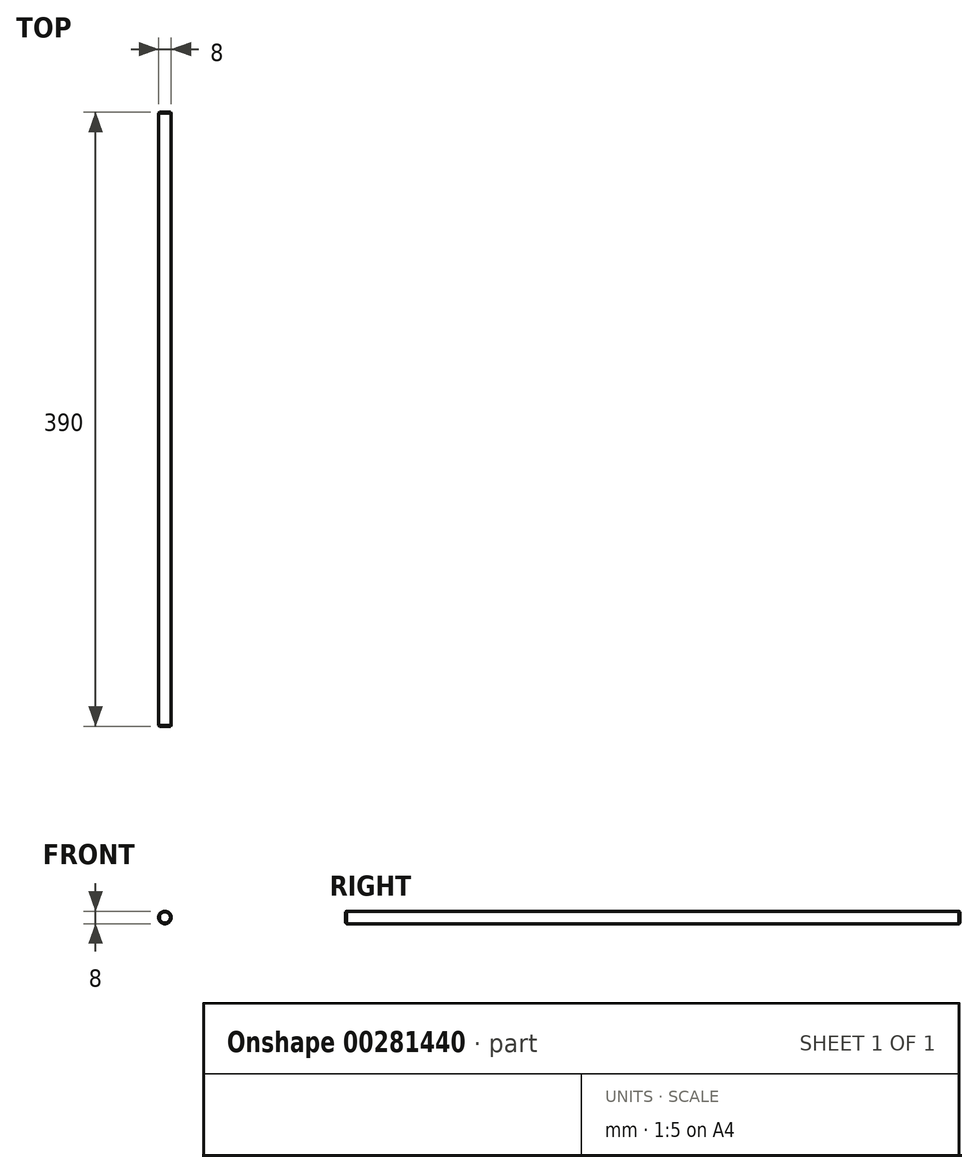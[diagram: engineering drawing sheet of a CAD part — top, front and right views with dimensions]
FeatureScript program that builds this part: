
annotation { "Feature Type Name" : "Feature", "Feature Type Description" : "" }
export const myFeature = defineFeature(function(context is Context, id is Id, definition is map)
    precondition{}
    {
        {
            var Q0;
            Q0=qCreatedBy(makeId("Front.planeOp"),FACE);
            var sketch = newSketch(context, id + "F0", { "sketchPlane" : qUnion([Q0])});
            skCircle(sketch, "E0", {"center": v(0, 0) * mm, "radius": 4 * mm});
            skSolve(sketch);
        }
        {
            var Q0;
            Q0=qSketchRegion(id+"F0",true);
            extrude(context, id + "F1", {"entities" : qUnion([Q0]), "endBound" : BoundingType.SYMMETRIC, "depth" : 390 * mm});
        }
        {
            var Q0;
            Q0=makeQuery(id+"F1.opExtrude","CAP_EDGE",EDGE,{"disambiguationData":[OSD([sQuery(id+"F0.wireOp",EDGE,"E0")])],"isStart":false});
            var Q1;
            Q1=makeQuery(id+"F1.opExtrude","CAP_EDGE",EDGE,{"disambiguationData":[OSD([sQuery(id+"F0.wireOp",EDGE,"E0")])],"isStart":true});
            chamfer(context, id + "F2", {"entities" : qUnion([Q0, Q1]), "width" : .5 * mm, "tangentPropagation" : true});
        }
    });
